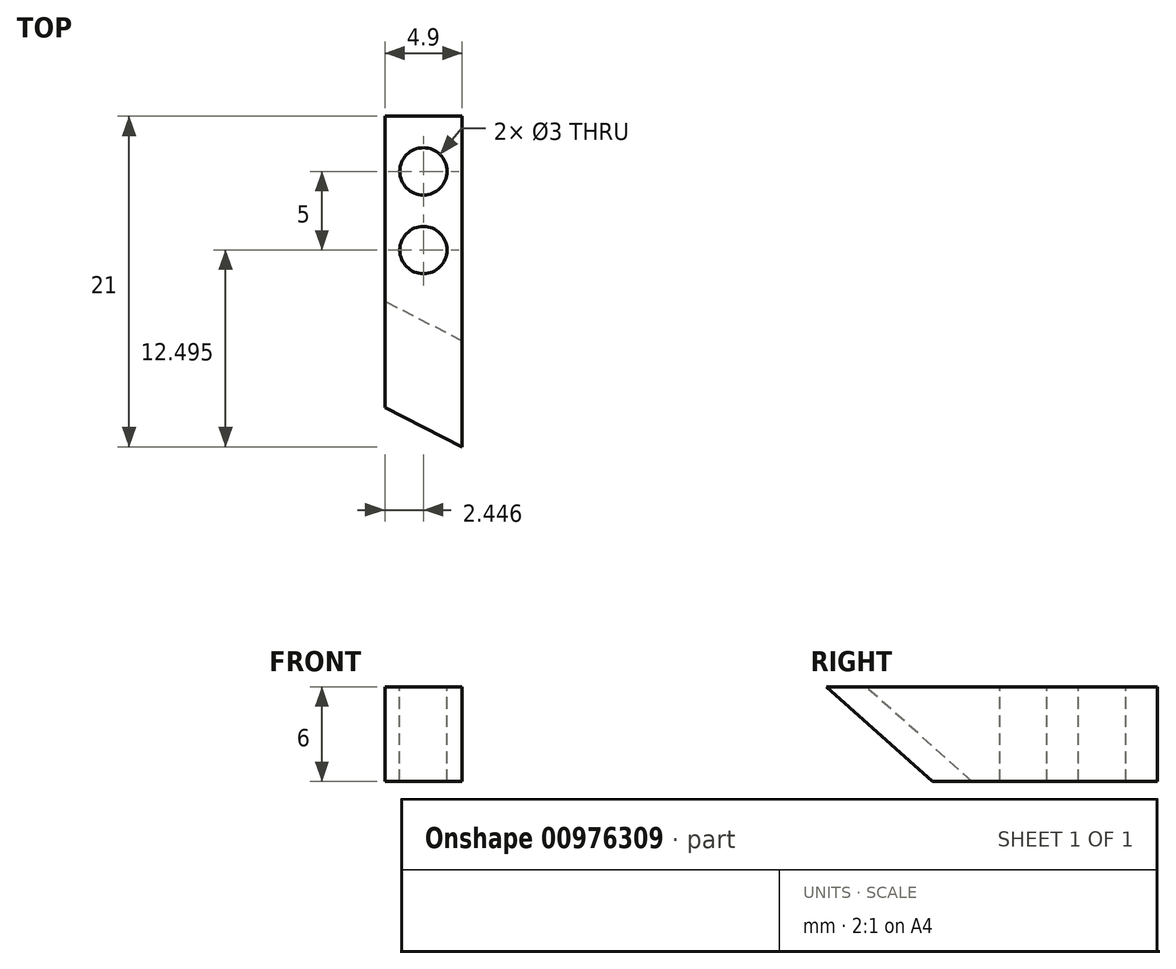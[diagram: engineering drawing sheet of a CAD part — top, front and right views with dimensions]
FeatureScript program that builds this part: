
annotation { "Feature Type Name" : "Feature", "Feature Type Description" : "" }
export const myFeature = defineFeature(function(context is Context, id is Id, definition is map)
    precondition{}
    {
        {
            var Q0;
            Q0=qCreatedBy(makeId("Top.planeOp"),FACE);
            var sketch = newSketch(context, id + "F0", { "sketchPlane" : qUnion([Q0])});
            skLineSegment(sketch, "E0.bottom", {"start": v(-372.54, 71.54) * mm, "end": v(-367.64, 71.54) * mm});
            skLineSegment(sketch, "E0.top", {"start": v(-372.54, 41.54) * mm, "end": v(-367.64, 41.54) * mm});
            skLineSegment(sketch, "E0.left", {"start": v(-372.54, 71.54) * mm, "end": v(-372.54, 41.54) * mm});
            skLineSegment(sketch, "E0.right", {"start": v(-367.64, 71.54) * mm, "end": v(-367.64, 41.54) * mm});
            skLineSegment(sketch, "E1", {"start": v(-367.64, 41.54) * mm, "end": v(-372.54, 44.04) * mm});
            skSolve(sketch);
        }
        {
            var Q0;
            {var subQ0=sQuery(id+"F0.wireOp",EDGE,"E0.bottom");Q0=makeQuery(id+"F0.imprint","IMPRINT",FACE,{"disambiguationData":[TD([[makeQuery(id+"F0.imprint","IMPRINT",EDGE,{"derivedFrom":subQ0}),-1.0]])]});}
            extrude(context, id + "F1", {"entities" : qUnion([Q0]), "depth" : 6 * mm, "offsetDistance" : 25 * mm});
        }
        {
            var Q0;
            Q0=makeQuery(id+"F1.opExtrude","CAP_EDGE",EDGE,{"disambiguationData":[OSD([sQuery(id+"F0.wireOp",EDGE,"E1")])],"isStart":true});
            chamfer(context, id + "F2", {"entities" : qUnion([Q0]), "width" : 6 * mm, "tangentPropagation" : true});
        }
        {
            var Q0;
            Q0=makeQuery(id+"F1.opExtrude","CAP_FACE",FACE,{"disambiguationData":[OSD([sQuery(id+"F0.wireOp",EDGE,"E0.bottom"),sQuery(id+"F0.wireOp",EDGE,"E0.left"),sQuery(id+"F0.wireOp",EDGE,"E0.right"),sQuery(id+"F0.wireOp",EDGE,"E1")])],"isStart":false});
            var sketch = newSketch(context, id + "F3", { "sketchPlane" : qUnion([Q0])});
            skLineSegment(sketch, "E2", {"start": v(-372.54, 62.54) * mm, "end": v(-367.64, 62.54) * mm});
            skCircle(sketch, "E3", {"center": v(-370.1, 59.04) * mm, "radius": 1.5 * mm});
            skCircle(sketch, "E4", {"center": v(-370.1, 54.04) * mm, "radius": 1.5 * mm});
            skSolve(sketch);
        }
        {
            var Q0;
            {var subQ0=sQuery(id+"F3.wireOp",EDGE,"E2");Q0=makeQuery(id+"F3.imprint","IMPRINT",FACE,{"disambiguationData":[TD([[makeQuery(id+"F3.imprint","IMPRINT",EDGE,{"derivedFrom":subQ0}),1.0]])]});}
            var Q1;
            Q1=makeQuery(id+"F3.imprint","IMPRINT",FACE,{"disambiguationData":[TD([[makeQuery(id+"F3.imprint","IMPRINT",EDGE,{"derivedFrom":sQuery(id+"F3.wireOp",EDGE,"E3")}),1.0]])]});
            var Q2;
            Q2=makeQuery(id+"F3.imprint","IMPRINT",FACE,{"disambiguationData":[TD([[makeQuery(id+"F3.imprint","IMPRINT",EDGE,{"derivedFrom":sQuery(id+"F3.wireOp",EDGE,"E4")}),1.0]])]});
            extrude(context, id + "F4", {"entities" : qUnion([Q0, Q1, Q2]), "operationType" : NewBodyOperationType.REMOVE, "endBound" : BoundingType.UP_TO_NEXT, "oppositeDirection" : true, "depth" : 11 * mm, "offsetDistance" : 25 * mm});
        }
    });
